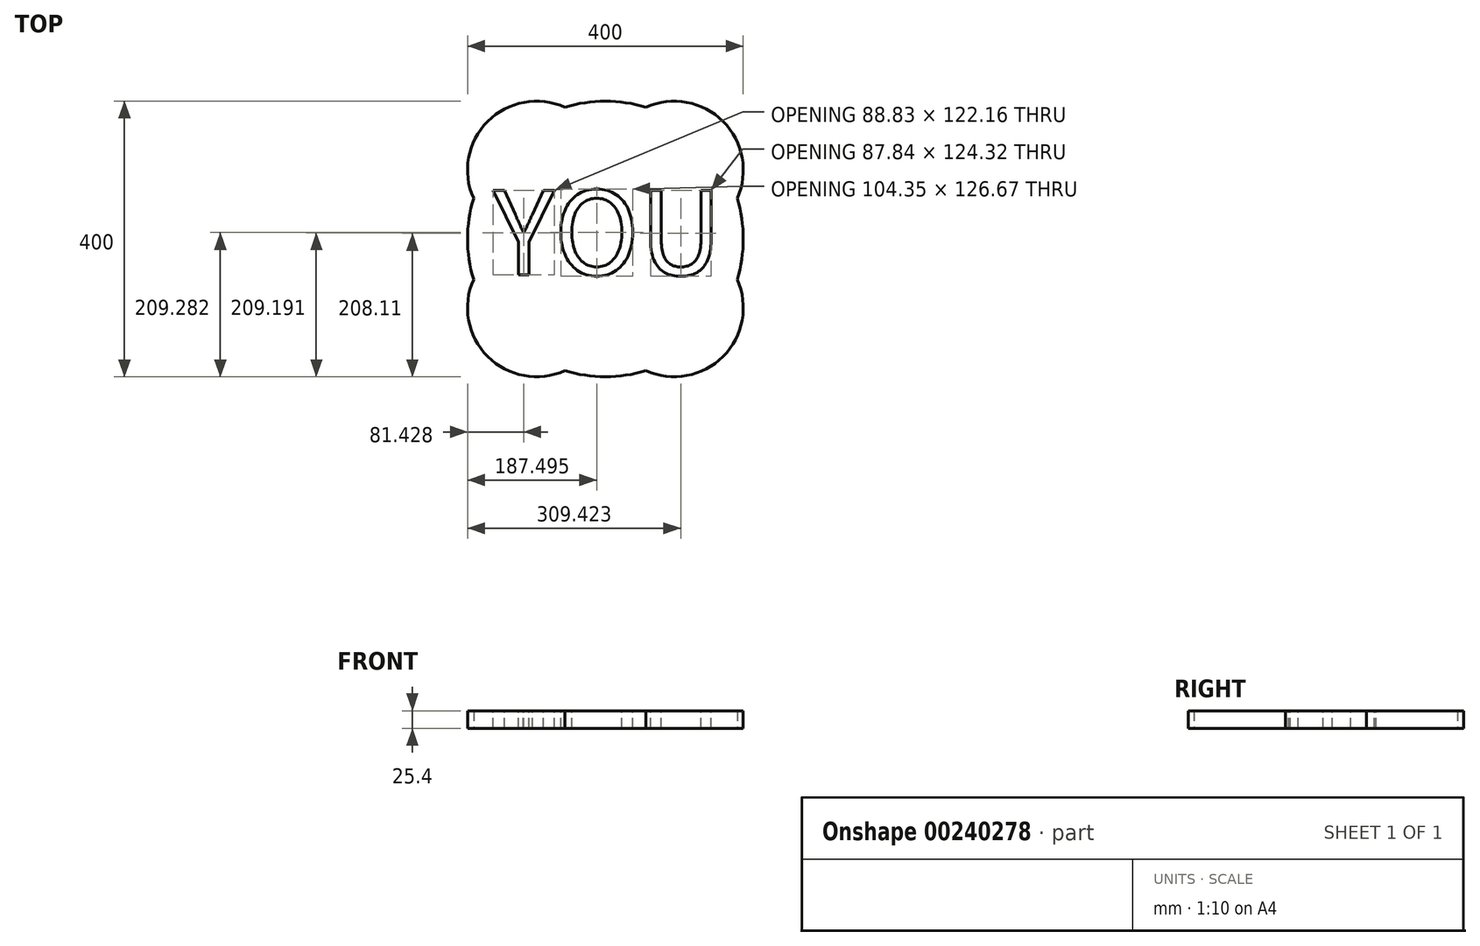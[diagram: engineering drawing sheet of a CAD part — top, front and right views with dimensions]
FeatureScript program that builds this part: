
annotation { "Feature Type Name" : "Feature", "Feature Type Description" : "" }
export const myFeature = defineFeature(function(context is Context, id is Id, definition is map)
    precondition{}
    {
        {
            var Q0;
            Q0=qCreatedBy(makeId("Top.planeOp"),FACE);
            var sketch = newSketch(context, id + "F0", { "sketchPlane" : qUnion([Q0])});
            skArc(sketch, "E0", {"start": v(58.86, 191.14) * mm, "mid": v(0, 200) * mm, "end": v(-58.86, 191.14) * mm});
            skArc(sketch, "E1", {"start": v(-58.86, 191.14) * mm, "mid": v(-170.71, 170.71) * mm, "end": v(-191.14, 58.86) * mm});
            skArc(sketch, "E2", {"start": v(-191.14, -58.86) * mm, "mid": v(-170.71, -170.71) * mm, "end": v(-58.86, -191.14) * mm});
            skArc(sketch, "E3", {"start": v(58.86, -191.14) * mm, "mid": v(170.71, -170.71) * mm, "end": v(191.14, -58.86) * mm});
            skArc(sketch, "E4.trimOffspring", {"start": v(191.14, 58.86) * mm, "mid": v(170.71, 170.71) * mm, "end": v(58.86, 191.14) * mm});
            skArc(sketch, "E5.trimOffspring", {"start": v(191.14, -58.86) * mm, "mid": v(200, 0) * mm, "end": v(191.14, 58.86) * mm});
            skArc(sketch, "E6.trimOffspring", {"start": v(-58.86, -191.14) * mm, "mid": v(0, -200) * mm, "end": v(58.86, -191.14) * mm});
            skArc(sketch, "E7.trimOffspring", {"start": v(-191.14, 58.86) * mm, "mid": v(-200, 0) * mm, "end": v(-191.14, -58.86) * mm});
            skSolve(sketch);
        }
        {
            var Q0;
            Q0 = qSketchRegion(id + "F0", true);
            extrude(context, id + "F1", {"entities" : qUnion([Q0]), "depth" : 25.4 * mm});
        }
        {
            var Q0;
            Q0=makeQuery(id+"F1.opExtrude","CAP_FACE",FACE,{"disambiguationData":[OSD([sQuery(id+"F0.wireOp",EDGE,"E0"),sQuery(id+"F0.wireOp",EDGE,"E1"),sQuery(id+"F0.wireOp",EDGE,"E2"),sQuery(id+"F0.wireOp",EDGE,"E3"),sQuery(id+"F0.wireOp",EDGE,"E4.trimOffspring"),sQuery(id+"F0.wireOp",EDGE,"E5.trimOffspring"),sQuery(id+"F0.wireOp",EDGE,"E6.trimOffspring"),sQuery(id+"F0.wireOp",EDGE,"E7.trimOffspring")])],"isStart":false});
            var sketch = newSketch(context, id + "F2", { "sketchPlane" : qUnion([Q0])});
            skArc(sketch, "E8.0", {"start": v(-196.47, 58.53) * mm, "mid": v(-205, 0) * mm, "end": v(-196.47, -58.53) * mm});
            skArc(sketch, "E8.1", {"start": v(-58.53, 196.47) * mm, "mid": v(-174.25, 174.25) * mm, "end": v(-196.47, 58.53) * mm});
            skArc(sketch, "E8.2", {"start": v(-196.47, -58.53) * mm, "mid": v(-174.25, -174.25) * mm, "end": v(-58.53, -196.47) * mm});
            skArc(sketch, "E8.3", {"start": v(58.53, 196.47) * mm, "mid": v(0, 205) * mm, "end": v(-58.53, 196.47) * mm});
            skArc(sketch, "E8.4", {"start": v(-58.53, -196.47) * mm, "mid": v(0, -205) * mm, "end": v(58.53, -196.47) * mm});
            skArc(sketch, "E8.5", {"start": v(58.53, -196.47) * mm, "mid": v(174.25, -174.25) * mm, "end": v(196.47, -58.53) * mm});
            skArc(sketch, "E8.6", {"start": v(196.47, -58.53) * mm, "mid": v(205, 0) * mm, "end": v(196.47, 58.53) * mm});
            skArc(sketch, "E8.7", {"start": v(196.47, 58.53) * mm, "mid": v(174.25, 174.25) * mm, "end": v(58.53, 196.47) * mm});
            skSolve(sketch);
        }
        {
            var Q0;
            Q0=makeQuery(id+"F2.imprint","IMPRINT",FACE,{"disambiguationData":[TD([[makeQuery(id+"F2.imprint","IMPRINT",EDGE,{"derivedFrom":makeQuery(id+"F1.opExtrude","CAP_EDGE",EDGE,{"disambiguationData":[OSD([sQuery(id+"F0.wireOp",EDGE,"E0")])],"isStart":false})}),1.0]])]});
            var sketch = newSketch(context, id + "F3", { "sketchPlane" : qUnion([Q0])});
            skText(sketch, "E9", { "text": "YOU", "fontName": "NotoSansCJKtc-Regular.otf"});
            const initialGuessF3  = {"E9": [-0.16283, -0.05189, 1, 0, 0.12]};
            skSetInitialGuess(sketch, initialGuessF3);
            skSolve(sketch);
        }
        {
            var Q0;
            Q0 = qSketchRegion(id + "F3", true);
            extrude(context, id + "F4", {"entities" : qUnion([Q0]), "operationType" : NewBodyOperationType.REMOVE, "oppositeDirection" : true, "depth" : 25.4 * mm});
        }
    });
